# Revit family: Lighting_Ceiling-Mounted_Focus_Yoyo_Ceiling
name_source: partatom
category: Lighting Fixtures
revit_build: Autodesk Revit 2017 (Build: 20190508_0315(x64)
units: mm (PartAtom-declared; Revit-internal decimal feet)

## family parameters
Cut with Voids When Loaded = No
Host = Face
Light Source = Yes
OmniClass Number = 23.80.70.00
OmniClass Title = Lighting
Part Type = Normal
Room Calculation Point = No
Round Connector Dimension = Use Diameter
Shared = No

## types (3) — shared parameters
AssetType = Fixed
BIMObjectName = Lighting_Ceiling-Mounted_Focus_Yoyo_Ceiling
Brand = Focus Lighting
Category = Indoor lighting
Color = Various
Color Filter = 16777215
Constituents = max 2 cables, 5x1.5 mm2
loop option in 5-pin clamp
2x2.5 mm2
Description = Yoyo is a new range of elegant indoor fixtures. The Yoyo luminaires are edge lit and are completely free of markings of internal components.
Design = C.F. Møller Architects
Dimming Lamp Color Temperature Shift = <None>
DurationUnit = Hours
ExpectedLife = 50000
Features = LED: Edge lit; Top reflector + Light guide plate (LGP)
Finish = Raw or painted aluminium
HasProtectiveEarth = No
IP_Code = IP20
IfcExportAs = IfcLightFixtureType
IfcExportType = NOTDEFINED
InsulationStandardClass = Class 2
LensMaterial = Acrylic, Clear
LightFixtureMountingType = Surface
LightFixturePlacingType = Ceiling
Manufacturer = Focus Lighting
ManufacturerName = Focus Lighting
ManufacturerURL = https://www.focus-lighting.dk
Material = Aluminium
NBSDescription = General purpose luminaires
NBSReference = 90-60-50/405
Name = Focus_Yoyo_Ceiling
NominalCurrent = 0 A
NominalFrequencyRange = 50 Hz
NominalHeight = 52 mm
NominalVoltage = 220 V
NominalVoltageCalc = 0 V
NumberOfPoles = 1
PhaseAngle = 0.00°
Photometric Web File = YOYO 350 500mA 16W 3000K CRI90 CDP Prismatisk.IES
ProductInformation = Yoyo is a new range of elegant indoor fixtures. The Yoyo luminaires are edge lit and are completely free of markings of internal components.
Shape = Sculptured
Tilt Angle = -90.00°
TotalWattage = 10 W
URL = https://focus-lighting.clients.ubivox.com
Uniclass2 = Pr_70_70_49
Uniclass2015Description = Surface luminaires
Uniclass2015Reference = Pr_70_70_48_85
UsageCurrent = 0 A
Version = 1
VersionDate = 18/06/2020
WarrantyDurationUnit = Year
zero-valued in all types: Default Elevation, ElectricalDeviceNominalPower, MaintenanceFactor, NumberOfSources

## per-type parameters (varying)
| type | ConvergoRefNr | Diameter | NominalDiameter | NominalLength | NominalRadius | NominalWidth | Size | Weight |
| Yoyo Ceiling - Ø225 | 0147-2006-0001-DK | Yoyo ceiling 225 | 225 mm  [stored 0.738189 ft] | 225 mm  [stored 0.738189 ft] | 113 mm | 225 mm  [stored 0.738189 ft] | 225x225x52 mm | 2 kg |
| Yoyo Ceiling - Ø350 | 0147-2006-0002-DK | Yoyo ceiling 350 | 350 mm  [stored 1.14829 ft] | 350 mm  [stored 1.14829 ft] | 175 mm  [stored 0.574147 ft] | 350 mm  [stored 1.14829 ft] | 350x350x52 mm | 2.1 kg |
| Yoyo Ceiling - Ø535 | 0147-2006-0003-DK | Yoyo ceiling 535 | 535 mm  [stored 1.75525 ft] | 535 mm  [stored 1.75525 ft] | 268 mm | 535 mm  [stored 1.75525 ft] | 535x535x52 mm | 2.2 kg |

note: column(s) folded — value = type name in every type: Model

note: [stored X ft] marks values corroborated as IEEE doubles in the binary element streams (Revit-internal decimal feet)

## geometry (parser evidence)
native form markers: Sweep x9
no freeform markers — native parametric forms only
